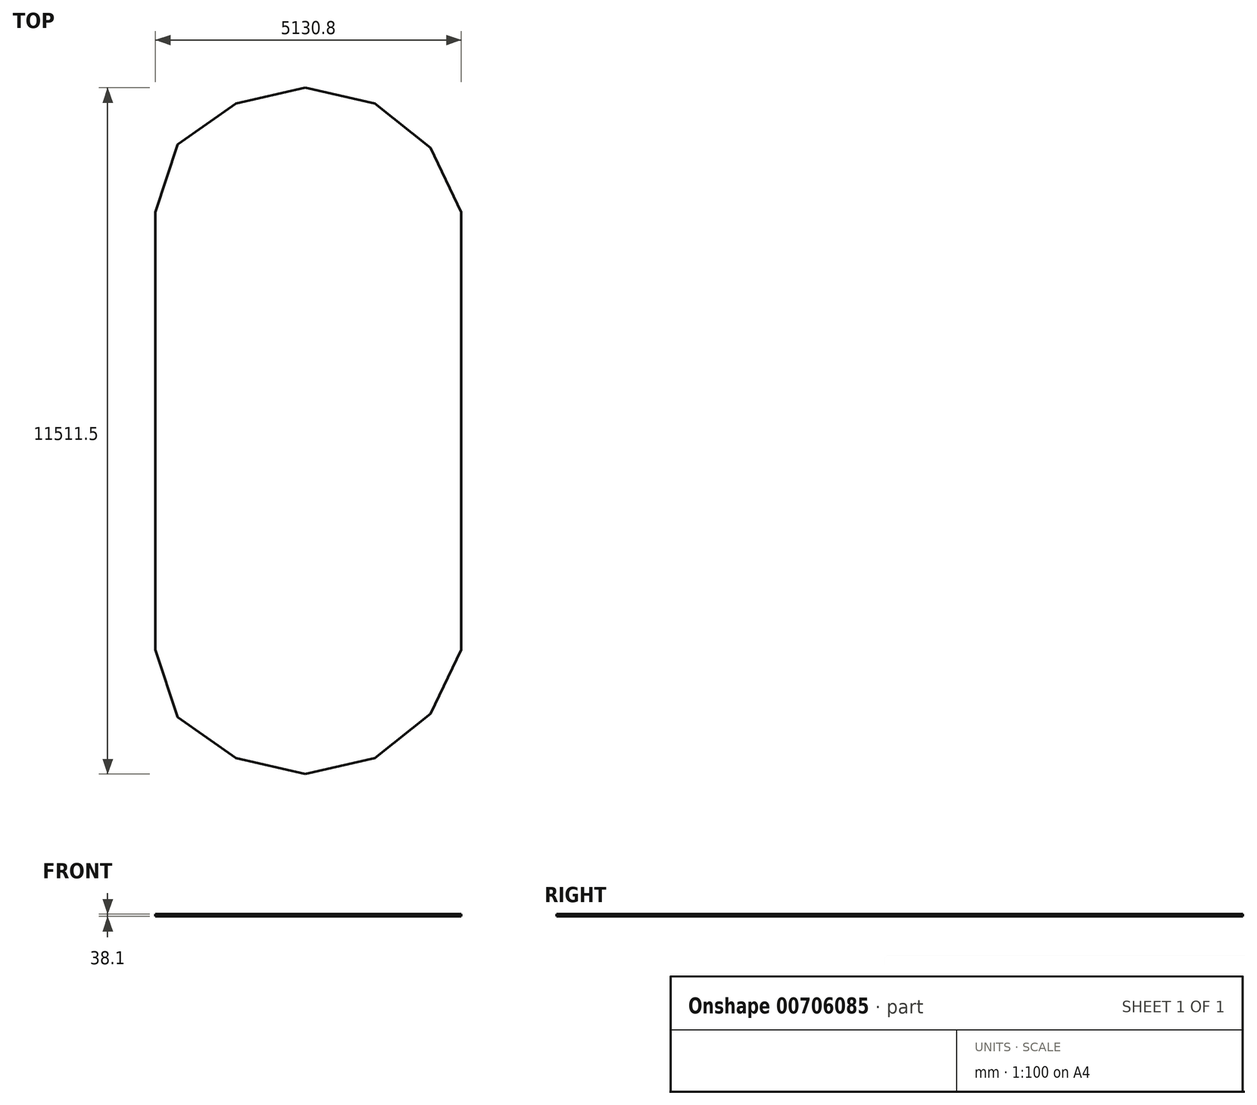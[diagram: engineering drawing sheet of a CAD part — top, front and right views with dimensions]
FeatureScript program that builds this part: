
annotation { "Feature Type Name" : "Feature", "Feature Type Description" : "" }
export const myFeature = defineFeature(function(context is Context, id is Id, definition is map)
    precondition{}
    {
        {
            var Q0;
            Q0=qCreatedBy(makeId("Top.planeOp"),FACE);
            var sketch = newSketch(context, id + "F0", { "sketchPlane" : qUnion([Q0])});
            skLineSegment(sketch, "E0", {"start": v(0, 0) * mm, "end": v(0, -3632.2) * mm});
            skLineSegment(sketch, "E1", {"start": v(0, -3632.2) * mm, "end": v(-3657.6, -3632.2) * mm});
            skLineSegment(sketch, "E2", {"start": v(-3657.6, -3632.2) * mm, "end": v(-3657.6, 1270) * mm});
            skLineSegment(sketch, "E3", {"start": v(-3657.6, 1270) * mm, "end": v(1854.2, 1270) * mm});
            skLineSegment(sketch, "E4", {"start": v(1854.2, 1270) * mm, "end": v(1854.2, 4673.6) * mm});
            skLineSegment(sketch, "E5", {"start": v(0, 0) * mm, "end": v(12649.2, 0) * mm});
            skLineSegment(sketch, "E6", {"start": v(12649.2, 0) * mm, "end": v(12649.2, 14209.95) * mm});
            skLineSegment(sketch, "E7", {"start": v(10849.53, 16794.74) * mm, "end": v(5515.53, 16794.74) * mm});
            skLineSegment(sketch, "E8", {"start": v(5515.53, 16794.74) * mm, "end": v(3073.4, 14209.95) * mm});
            skLineSegment(sketch, "E9", {"start": v(3073.4, 14209.95) * mm, "end": v(3073.4, 4673.6) * mm});
            skLineSegment(sketch, "E10", {"start": v(1854.2, 4673.6) * mm, "end": v(3073.4, 4673.6) * mm});
            skLineSegment(sketch, "E11", {"start": v(6223, 12575.67) * mm, "end": v(6223, 5235.07) * mm});
            skLineSegment(sketch, "E12", {"start": v(11353.8, 5235.07) * mm, "end": v(11353.8, 12575.67) * mm});
            skLineSegment(sketch, "E13", {"start": v(11353.8, 12575.67) * mm, "end": v(10835.82, 13651.24) * mm});
            skLineSegment(sketch, "E14", {"start": v(10835.82, 13651.24) * mm, "end": v(9902.45, 14395.54) * mm});
            skLineSegment(sketch, "E15", {"start": v(9902.45, 14395.54) * mm, "end": v(8738.57, 14661.14) * mm});
            skLineSegment(sketch, "E16", {"start": v(8738.57, 14661.14) * mm, "end": v(7574.69, 14395.54) * mm});
            skLineSegment(sketch, "E17", {"start": v(7574.69, 14395.54) * mm, "end": v(6598.03, 13709.03) * mm});
            skLineSegment(sketch, "E18", {"start": v(6598.03, 13709.03) * mm, "end": v(6223, 12575.67) * mm});
            skLineSegment(sketch, "E19", {"start": v(6223, 8905.37) * mm, "end": v(11353.8, 8905.37) * mm});
            skLineSegment(sketch, "E20.MirrorCS", {"start": v(6598.03, 4101.7) * mm, "end": v(6223, 5235.07) * mm});
            skLineSegment(sketch, "E21.MirrorCS", {"start": v(7574.69, 3415.2) * mm, "end": v(6598.03, 4101.7) * mm});
            skLineSegment(sketch, "E22.MirrorCS", {"start": v(8738.57, 3149.6) * mm, "end": v(7574.69, 3415.2) * mm});
            skLineSegment(sketch, "E23.MirrorCS", {"start": v(9902.45, 3415.2) * mm, "end": v(8738.57, 3149.6) * mm});
            skLineSegment(sketch, "E24.MirrorCS", {"start": v(10835.82, 4159.5) * mm, "end": v(9902.45, 3415.2) * mm});
            skLineSegment(sketch, "E25.MirrorCS", {"start": v(11353.8, 5235.07) * mm, "end": v(10835.82, 4159.5) * mm});
            skLineSegment(sketch, "E26", {"start": v(10849.53, 16794.74) * mm, "end": v(12649.2, 14209.95) * mm});
            skSolve(sketch);
        }
        {
            var Q0;
            {var subQ0=sQuery(id+"F0.wireOp",EDGE,"E19");Q0=makeQuery(id+"F0.imprint","IMPRINT",FACE,{"disambiguationData":[TD([[makeQuery(id+"F0.imprint","IMPRINT",EDGE,{"derivedFrom":subQ0}),-1.0]])]});}
            var Q1;
            {var subQ0=sQuery(id+"F0.wireOp",EDGE,"E13");Q1=makeQuery(id+"F0.imprint","IMPRINT",FACE,{"disambiguationData":[TD([[makeQuery(id+"F0.imprint","IMPRINT",EDGE,{"derivedFrom":subQ0}),1.0]])]});}
            extrude(context, id + "F1", {"entities" : qUnion([Q0, Q1]), "depth" : 38.1 * mm, "offsetDistance" : 25.4 * mm});
        }
    });
